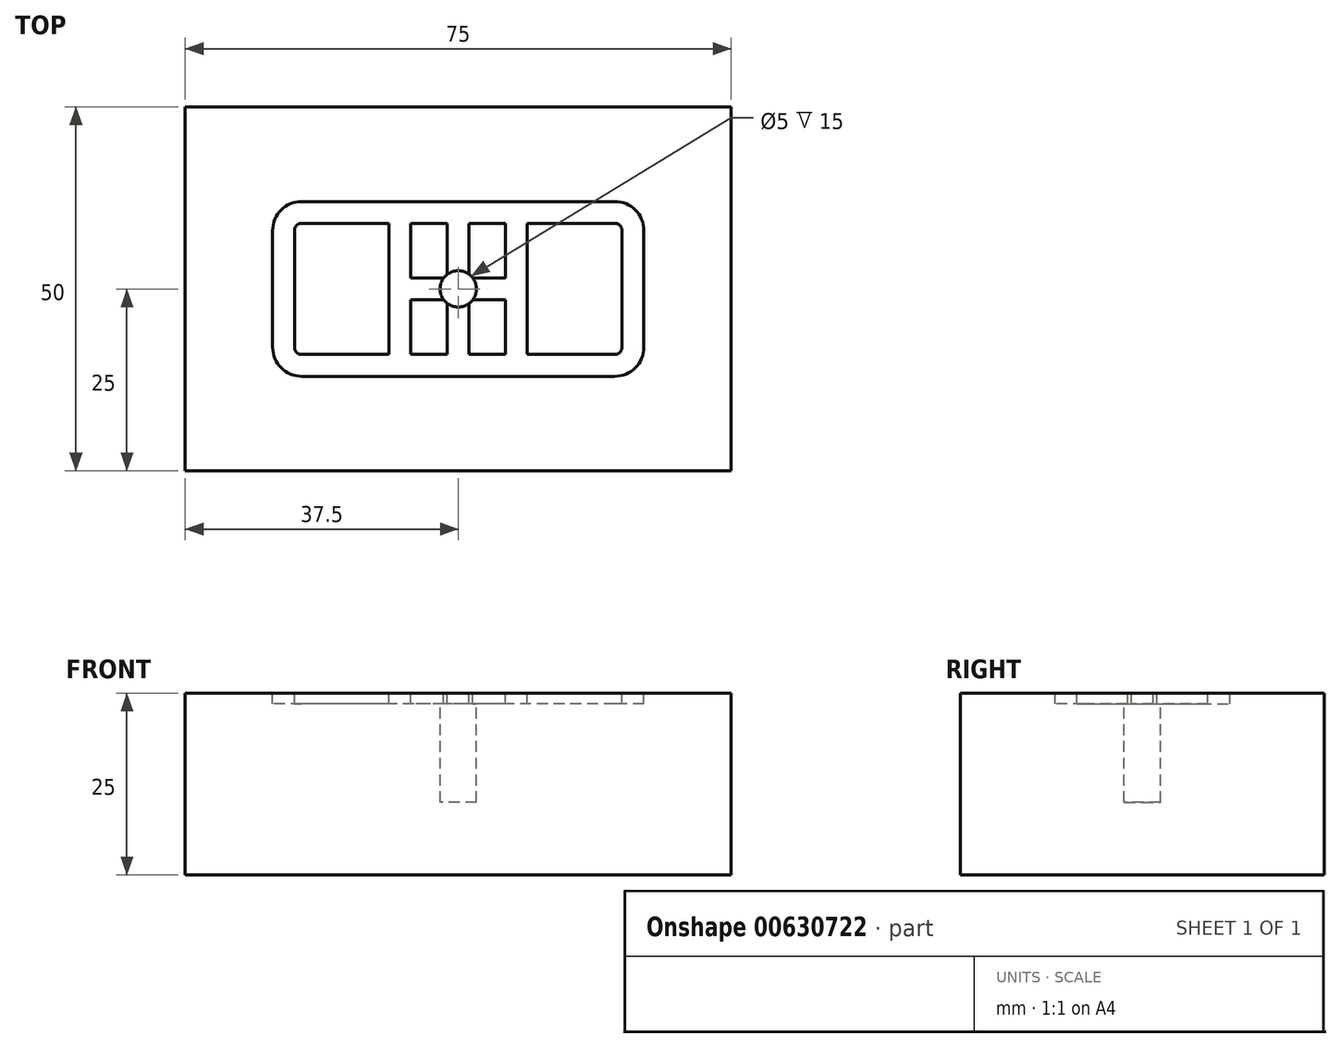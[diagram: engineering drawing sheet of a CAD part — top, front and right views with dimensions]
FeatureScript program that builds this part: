
annotation { "Feature Type Name" : "Feature", "Feature Type Description" : "" }
export const myFeature = defineFeature(function(context is Context, id is Id, definition is map)
    precondition{}
    {
        {
            var Q0;
            Q0=qCreatedBy(makeId("Top.planeOp"),FACE);
            var sketch = newSketch(context, id + "F0", { "sketchPlane" : qUnion([Q0])});
            skLineSegment(sketch, "E0.bottom", {"start": v(37.5, -25) * mm, "end": v(-37.5, -25) * mm});
            skLineSegment(sketch, "E0.top", {"start": v(37.5, 25) * mm, "end": v(-37.5, 25) * mm});
            skLineSegment(sketch, "E0.left", {"start": v(37.5, -25) * mm, "end": v(37.5, 25) * mm});
            skLineSegment(sketch, "E0.right", {"start": v(-37.5, -25) * mm, "end": v(-37.5, 25) * mm});
            skPoint(sketch, "E0.middle", {"position": v(0, 0) * mm});
            skSolve(sketch);
        }
        {
            var Q0;
            Q0=makeQuery(id+"F0.imprint","IMPRINT",FACE,{"disambiguationData":[TD([[makeQuery(id+"F0.imprint","IMPRINT",EDGE,{"derivedFrom":sQuery(id+"F0.wireOp",EDGE,"E0.bottom")}),-1.0]])]});
            extrude(context, id + "F1", {"entities" : qUnion([Q0]), "depth" : 25 * mm, "offsetDistance" : 25 * mm});
        }
        {
            var Q0;
            Q0=makeQuery(id+"F1.opExtrude","CAP_FACE",FACE,{"disambiguationData":[OSD([sQuery(id+"F0.wireOp",EDGE,"E0.bottom"),sQuery(id+"F0.wireOp",EDGE,"E0.top"),sQuery(id+"F0.wireOp",EDGE,"E0.left"),sQuery(id+"F0.wireOp",EDGE,"E0.right")])],"isStart":false});
            var sketch = newSketch(context, id + "F2", { "sketchPlane" : qUnion([Q0])});
            skLineSegment(sketch, "E1.bottom", {"start": v(6.5, -9) * mm, "end": v(1.5, -9) * mm});
            skLineSegment(sketch, "E1.top", {"start": v(6.5, 9) * mm, "end": v(1.5, 9) * mm});
            skLineSegment(sketch, "E1.left", {"start": v(6.5, -9) * mm, "end": v(6.5, -1.5) * mm});
            skLineSegment(sketch, "E1.right", {"start": v(-6.5, -9) * mm, "end": v(-6.5, -1.5) * mm});
            skPoint(sketch, "E1.middle", {"position": v(0, 0) * mm});
            skLineSegment(sketch, "E2.bottom", {"start": v(21.5, -9) * mm, "end": v(9.5, -9) * mm});
            skLineSegment(sketch, "E2.top", {"start": v(21.5, 9) * mm, "end": v(9.5, 9) * mm});
            skLineSegment(sketch, "E2.left", {"start": v(22.5, -8) * mm, "end": v(22.5, 8) * mm});
            skLineSegment(sketch, "E2.right", {"start": v(9.5, -9) * mm, "end": v(9.5, 9) * mm});
            skPoint(sketch, "E2.middle", {"position": v(16, 0) * mm});
            skLineSegment(sketch, "E3.bottom", {"start": v(-9.5, -9) * mm, "end": v(-21.5, -9) * mm});
            skLineSegment(sketch, "E3.top", {"start": v(-9.5, 9) * mm, "end": v(-21.5, 9) * mm});
            skLineSegment(sketch, "E3.left", {"start": v(-9.5, -9) * mm, "end": v(-9.5, 9) * mm});
            skLineSegment(sketch, "E3.right", {"start": v(-22.5, -8) * mm, "end": v(-22.5, 8) * mm});
            skPoint(sketch, "E3.middle", {"position": v(-16, 0) * mm});
            skLineSegment(sketch, "E4.bottom", {"start": v(21.5, -12) * mm, "end": v(-21.5, -12) * mm});
            skLineSegment(sketch, "E4.top", {"start": v(21.5, 12) * mm, "end": v(-21.5, 12) * mm});
            skLineSegment(sketch, "E4.left", {"start": v(25.5, -8) * mm, "end": v(25.5, 8) * mm});
            skLineSegment(sketch, "E4.right", {"start": v(-25.5, -8) * mm, "end": v(-25.5, 8) * mm});
            skLineSegment(sketch, "E5.bottom", {"start": v(6.5, -1.5) * mm, "end": v(1.5, -1.5) * mm});
            skLineSegment(sketch, "E5.top", {"start": v(6.5, 1.5) * mm, "end": v(1.5, 1.5) * mm});
            skLineSegment(sketch, "E6.left", {"start": v(1.5, 9) * mm, "end": v(1.5, 1.5) * mm});
            skLineSegment(sketch, "E6.right", {"start": v(-1.5, 9) * mm, "end": v(-1.5, 1.5) * mm});
            skLineSegment(sketch, "E7.trimOffspring", {"start": v(-1.5, -1.5) * mm, "end": v(-1.5, -9) * mm});
            skLineSegment(sketch, "E8.trimOffspring", {"start": v(-1.5, 1.5) * mm, "end": v(-6.5, 1.5) * mm});
            skLineSegment(sketch, "E9.trimOffspring", {"start": v(1.5, -1.5) * mm, "end": v(1.5, -9) * mm});
            skLineSegment(sketch, "E10.trimOffspring", {"start": v(-6.5, 1.5) * mm, "end": v(-6.5, 9) * mm});
            skLineSegment(sketch, "E11.trimOffspring", {"start": v(-1.5, -9) * mm, "end": v(-6.5, -9) * mm});
            skLineSegment(sketch, "E12.trimOffspring", {"start": v(6.5, 1.5) * mm, "end": v(6.5, 9) * mm});
            skLineSegment(sketch, "E13.trimOffspring", {"start": v(-1.5, 9) * mm, "end": v(-6.5, 9) * mm});
            skPoint(sketch, "E14.visualSharp", {"position": v(22.5, 9) * mm});
            skArc(sketch, "E14.filletArc", {"start": v(22.5, 8) * mm, "mid": v(22.2, 8.7) * mm, "end": v(21.5, 9) * mm});
            skPoint(sketch, "E15.visualSharp", {"position": v(22.5, -9) * mm});
            skArc(sketch, "E15.filletArc", {"start": v(21.5, -9) * mm, "mid": v(22.2, -8.7) * mm, "end": v(22.5, -8) * mm});
            skPoint(sketch, "E16.visualSharp", {"position": v(-22.5, -9) * mm});
            skArc(sketch, "E16.filletArc", {"start": v(-22.5, -8) * mm, "mid": v(-22.2, -8.7) * mm, "end": v(-21.5, -9) * mm});
            skPoint(sketch, "E17.visualSharp", {"position": v(-22.5, 9) * mm});
            skArc(sketch, "E17.filletArc", {"start": v(-21.5, 9) * mm, "mid": v(-22.2, 8.7) * mm, "end": v(-22.5, 8) * mm});
            skPoint(sketch, "E18.visualSharp", {"position": v(-25.5, 12) * mm});
            skArc(sketch, "E18.filletArc", {"start": v(-21.5, 12) * mm, "mid": v(-24.33, 10.83) * mm, "end": v(-25.5, 8) * mm});
            skPoint(sketch, "E19.visualSharp", {"position": v(25.5, 12) * mm});
            skArc(sketch, "E19.filletArc", {"start": v(25.5, 8) * mm, "mid": v(24.33, 10.83) * mm, "end": v(21.5, 12) * mm});
            skPoint(sketch, "E20.visualSharp", {"position": v(25.5, -12) * mm});
            skArc(sketch, "E20.filletArc", {"start": v(21.5, -12) * mm, "mid": v(24.33, -10.83) * mm, "end": v(25.5, -8) * mm});
            skPoint(sketch, "E21.visualSharp", {"position": v(-25.5, -12) * mm});
            skArc(sketch, "E21.filletArc", {"start": v(-25.5, -8) * mm, "mid": v(-24.33, -10.83) * mm, "end": v(-21.5, -12) * mm});
            skLineSegment(sketch, "E22.trimOffspring", {"start": v(-1.5, -1.5) * mm, "end": v(-6.5, -1.5) * mm});
            skSolve(sketch);
        }
        {
            var Q0;
            Q0 = qSketchRegion(id + "F2", true);
            extrude(context, id + "F3", {"entities" : qUnion([Q0]), "operationType" : NewBodyOperationType.REMOVE, "oppositeDirection" : true, "depth" : 1.5 * mm, "offsetDistance" : 25 * mm});
        }
        {
            var Q0;
            {var subQ0=sQuery(id+"F0.wireOp",EDGE,"E0.bottom");var subQ1=sQuery(id+"F0.wireOp",EDGE,"E0.right");var subQ2=sQuery(id+"F0.wireOp",EDGE,"E0.top");var subQ3=sQuery(id+"F0.wireOp",EDGE,"E0.left");Q0=makeQuery(id+"F3.boolean.opBoolean","SPLIT",FACE,{"disambiguationData":[TD([makeQuery(id+"F1.opExtrude","SWEPT_FACE",FACE,{"disambiguationData":[OSD([subQ0])]})])],"derivedFrom":makeQuery(id+"F1.opExtrude","CAP_FACE",FACE,{"disambiguationData":[OSD([subQ0,subQ2,subQ3,subQ1])],"isStart":false})});}
            var sketch = newSketch(context, id + "F4", { "sketchPlane" : qUnion([Q0])});
            skCircle(sketch, "E23", {"center": v(0, 0) * mm, "radius": 2.5 * mm});
            skSolve(sketch);
        }
        {
            var Q0;
            Q0 = qSketchRegion(id + "F4", true);
            extrude(context, id + "F5", {"entities" : qUnion([Q0]), "operationType" : NewBodyOperationType.REMOVE, "oppositeDirection" : true, "depth" : 15 * mm, "offsetDistance" : 25 * mm});
        }
    });
